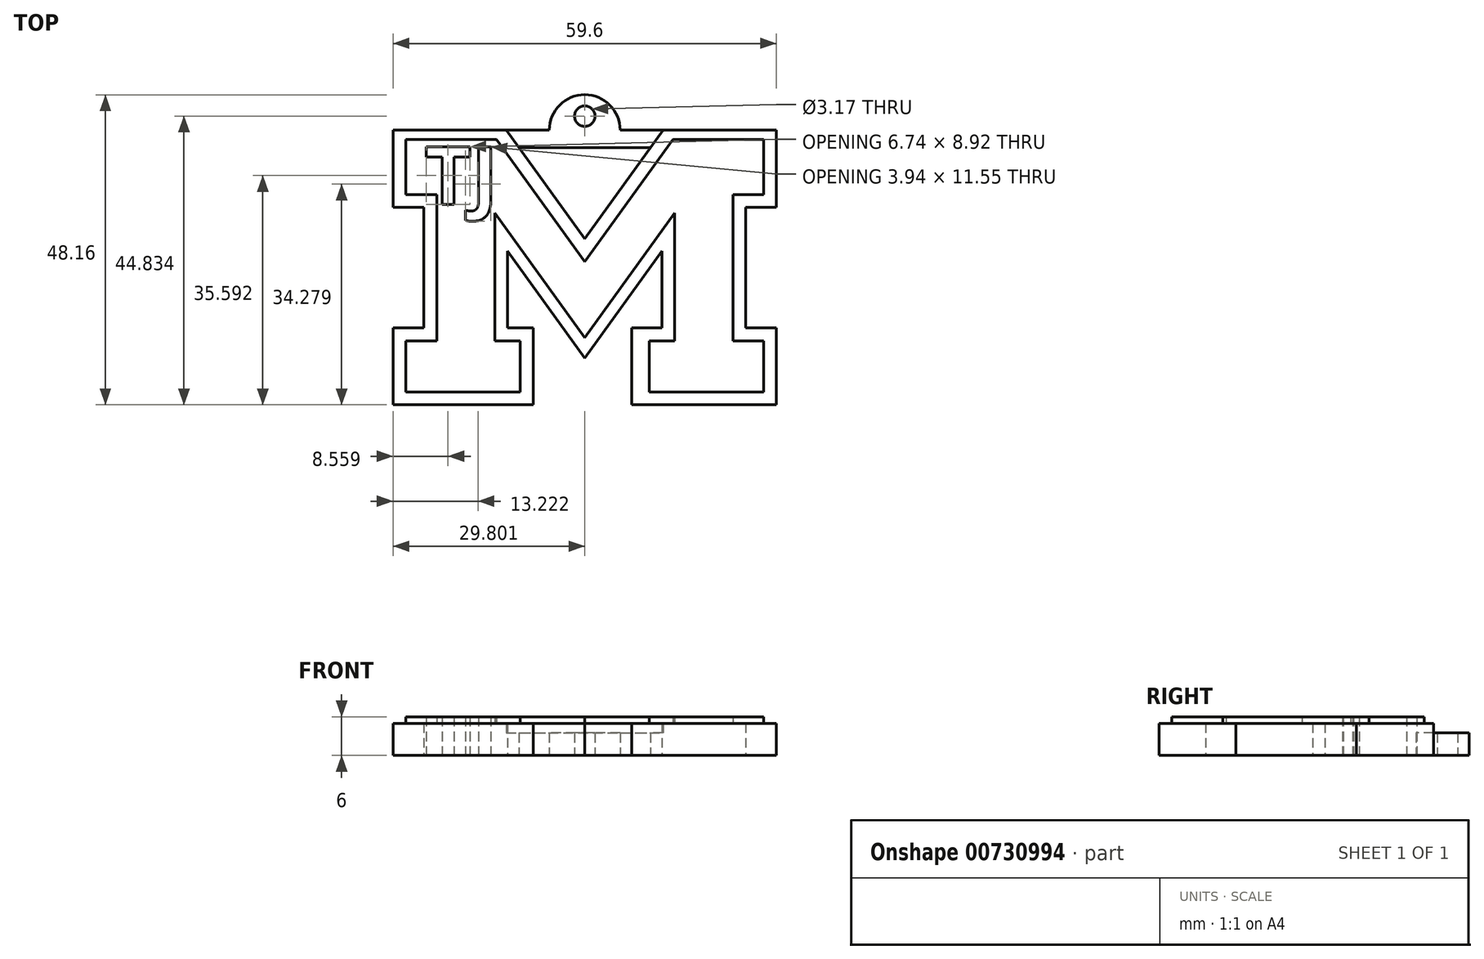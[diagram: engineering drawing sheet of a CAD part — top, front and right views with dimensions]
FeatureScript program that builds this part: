
annotation { "Feature Type Name" : "Feature", "Feature Type Description" : "" }
export const myFeature = defineFeature(function(context is Context, id is Id, definition is map)
    precondition{}
    {
        {
            var Q0;
            Q0=qCreatedBy(makeId("Top.planeOp"),FACE);
            var sketch = newSketch(context, id + "F0", { "sketchPlane" : qUnion([Q0])});
            skLineSegment(sketch, "E0", {"start": v(-32.04, 11.43) * mm, "end": v(-32.04, 23.43) * mm});
            skLineSegment(sketch, "E1", {"start": v(-32.04, 23.43) * mm, "end": v(-14.43, 23.43) * mm});
            skLineSegment(sketch, "E2", {"start": v(-14.43, 23.43) * mm, "end": v(-2.24, 6.55) * mm});
            skLineSegment(sketch, "E3", {"start": v(-32.04, 11.43) * mm, "end": v(-27.26, 11.43) * mm});
            skLineSegment(sketch, "E4", {"start": v(-27.26, 11.43) * mm, "end": v(-27.26, -7.3) * mm});
            skLineSegment(sketch, "E5", {"start": v(-27.26, -7.3) * mm, "end": v(-32.04, -7.3) * mm});
            skLineSegment(sketch, "E6", {"start": v(-32.04, -7.3) * mm, "end": v(-32.04, -19.23) * mm});
            skLineSegment(sketch, "E7", {"start": v(-32.04, -19.23) * mm, "end": v(-10.26, -19.23) * mm});
            skLineSegment(sketch, "E8", {"start": v(-10.26, -19.23) * mm, "end": v(-10.26, -7.3) * mm});
            skLineSegment(sketch, "E9", {"start": v(-10.26, -7.3) * mm, "end": v(-14.24, -7.3) * mm});
            skLineSegment(sketch, "E10", {"start": v(-14.24, -7.3) * mm, "end": v(-14.24, 4.63) * mm});
            skLineSegment(sketch, "E11", {"start": v(-14.24, 4.63) * mm, "end": v(-2.24, -11.98) * mm});
            skLineSegment(sketch, "E12.MirrorCS", {"start": v(9.95, 23.43) * mm, "end": v(-2.24, 6.55) * mm});
            skLineSegment(sketch, "E13.MirrorCS", {"start": v(9.76, 4.63) * mm, "end": v(-2.24, -11.98) * mm});
            skLineSegment(sketch, "E14.MirrorCS", {"start": v(9.76, -7.3) * mm, "end": v(9.76, 4.63) * mm});
            skLineSegment(sketch, "E15.MirrorCS", {"start": v(5.07, -7.3) * mm, "end": v(9.76, -7.3) * mm});
            skLineSegment(sketch, "E16.MirrorCS", {"start": v(5.07, -19.23) * mm, "end": v(5.07, -7.3) * mm});
            skLineSegment(sketch, "E17.MirrorCS", {"start": v(27.56, -19.23) * mm, "end": v(5.07, -19.23) * mm});
            skLineSegment(sketch, "E18.MirrorCS", {"start": v(27.56, -7.3) * mm, "end": v(27.56, -19.23) * mm});
            skLineSegment(sketch, "E19.MirrorCS", {"start": v(22.78, -7.3) * mm, "end": v(27.56, -7.3) * mm});
            skLineSegment(sketch, "E20.MirrorCS", {"start": v(22.78, 11.43) * mm, "end": v(22.78, -7.3) * mm});
            skLineSegment(sketch, "E21.MirrorCS", {"start": v(27.56, 11.43) * mm, "end": v(22.78, 11.43) * mm});
            skLineSegment(sketch, "E22.MirrorCS", {"start": v(27.56, 11.43) * mm, "end": v(27.56, 23.43) * mm});
            skLineSegment(sketch, "E23.MirrorCS", {"start": v(27.56, 23.43) * mm, "end": v(9.95, 23.43) * mm});
            skLineSegment(sketch, "E24", {"start": v(-14.43, 23.43) * mm, "end": v(9.95, 23.43) * mm});
            skLineSegment(sketch, "E25", {"start": v(-12.46, 20.71) * mm, "end": v(7.98, 20.71) * mm});
            skArc(sketch, "E26", {"start": v(3.26, 23.43) * mm, "mid": v(-2.24, 28.93) * mm, "end": v(-7.74, 23.43) * mm});
            skCircle(sketch, "E27", {"center": v(-2.24, 25.6) * mm, "radius": 1.59 * mm});
            skLineSegment(sketch, "E28", {"start": v(-30.04, 22) * mm, "end": v(-30.04, 13.43) * mm});
            skLineSegment(sketch, "E29", {"start": v(-30.04, 13.43) * mm, "end": v(-25.26, 13.43) * mm});
            skLineSegment(sketch, "E30", {"start": v(-25.26, 13.43) * mm, "end": v(-25.26, -9.3) * mm});
            skLineSegment(sketch, "E31", {"start": v(-25.26, -9.3) * mm, "end": v(-30.04, -9.3) * mm});
            skLineSegment(sketch, "E32", {"start": v(-30.04, -9.3) * mm, "end": v(-30.04, -17.23) * mm});
            skLineSegment(sketch, "E33", {"start": v(-30.04, -17.23) * mm, "end": v(-12.26, -17.23) * mm});
            skLineSegment(sketch, "E34", {"start": v(-12.26, -17.23) * mm, "end": v(-12.26, -9.3) * mm});
            skLineSegment(sketch, "E35", {"start": v(-12.26, -9.3) * mm, "end": v(-16.24, -9.3) * mm});
            skLineSegment(sketch, "E36", {"start": v(-16.24, -9.3) * mm, "end": v(-16.24, 10.56) * mm});
            skLineSegment(sketch, "E37", {"start": v(-16.24, 10.56) * mm, "end": v(-2.24, -8.82) * mm});
            skLineSegment(sketch, "E38", {"start": v(-30.04, 22) * mm, "end": v(-15.94, 22) * mm});
            skLineSegment(sketch, "E39", {"start": v(-15.94, 22) * mm, "end": v(-2.24, 3.02) * mm});
            skLineSegment(sketch, "E40.MirrorCS", {"start": v(11.46, 22) * mm, "end": v(-2.24, 3.02) * mm});
            skLineSegment(sketch, "E41.MirrorCS", {"start": v(11.76, 10.56) * mm, "end": v(-2.24, -8.82) * mm});
            skLineSegment(sketch, "E42.MirrorCS", {"start": v(11.76, -9.3) * mm, "end": v(11.76, 10.56) * mm});
            skLineSegment(sketch, "E43.MirrorCS", {"start": v(25.56, 22) * mm, "end": v(11.46, 22) * mm});
            skLineSegment(sketch, "E44.MirrorCS", {"start": v(25.56, 22) * mm, "end": v(25.56, 13.43) * mm});
            skLineSegment(sketch, "E45.MirrorCS", {"start": v(20.78, 13.43) * mm, "end": v(20.78, -9.3) * mm});
            skLineSegment(sketch, "E46.MirrorCS", {"start": v(25.56, 13.43) * mm, "end": v(20.78, 13.43) * mm});
            skLineSegment(sketch, "E47.MirrorCS", {"start": v(20.78, -9.3) * mm, "end": v(25.56, -9.3) * mm});
            skLineSegment(sketch, "E48.MirrorCS", {"start": v(25.56, -9.3) * mm, "end": v(25.56, -17.23) * mm});
            skLineSegment(sketch, "E49.MirrorCS", {"start": v(7.78, -17.23) * mm, "end": v(7.78, -9.3) * mm});
            skLineSegment(sketch, "E50.MirrorCS", {"start": v(7.78, -9.3) * mm, "end": v(11.76, -9.3) * mm});
            skLineSegment(sketch, "E51.MirrorCS", {"start": v(25.56, -17.23) * mm, "end": v(7.78, -17.23) * mm});
            skText(sketch, "E52", { "text": "TJ", "fontName": "OpenSans-Bold.ttf"});
            const initialGuessF0  = {"E52": [-0.0271, 0.0119, 1, 0, 0.009]};
            skSetInitialGuess(sketch, initialGuessF0);
            skSolve(sketch);
        }
        {
            var Q0;
            Q0=makeQuery(id+"F0.imprint","IMPRINT",FACE,{"disambiguationData":[TD([[makeQuery(id+"F0.imprint","IMPRINT",EDGE,{"derivedFrom":sQuery(id+"F0.wireOp",EDGE,"E28")}),1.0]])]});
            extrude(context, id + "F1", {"entities" : qUnion([Q0]), "depth" : 6 * mm, "offsetDistance" : 25 * mm});
        }
        {
            var Q0;
            Q0=makeQuery(id+"F0.imprint","IMPRINT",FACE,{"disambiguationData":[TD([[makeQuery(id+"F0.imprint","IMPRINT",EDGE,{"derivedFrom":sQuery(id+"F0.wireOp",EDGE,"E0")}),-1.0]])]});
            extrude(context, id + "F2", {"entities" : qUnion([Q0]), "operationType" : NewBodyOperationType.ADD, "depth" : 5 * mm, "offsetDistance" : 25 * mm});
        }
        {
            var Q0;
            {var subQ7=sQuery(id+"F0.wireOp",EDGE,"E25");Q0=makeQuery(id+"F0.imprint","IMPRINT",FACE,{"disambiguationData":[TD([[makeQuery(id+"F0.imprint","IMPRINT",EDGE,{"derivedFrom":subQ7}),1.0]])]});}
            var Q1;
            {var subQ0=sQuery(id+"F0.wireOp",EDGE,"E26");Q1=makeQuery(id+"F0.imprint","IMPRINT",FACE,{"disambiguationData":[TD([[makeQuery(id+"F0.imprint","IMPRINT",EDGE,{"derivedFrom":subQ0}),1.0]])]});}
            extrude(context, id + "F3", {"entities" : qUnion([Q0, Q1]), "operationType" : NewBodyOperationType.ADD, "depth" : 3.5 * mm, "offsetDistance" : 25 * mm});
        }
    });
